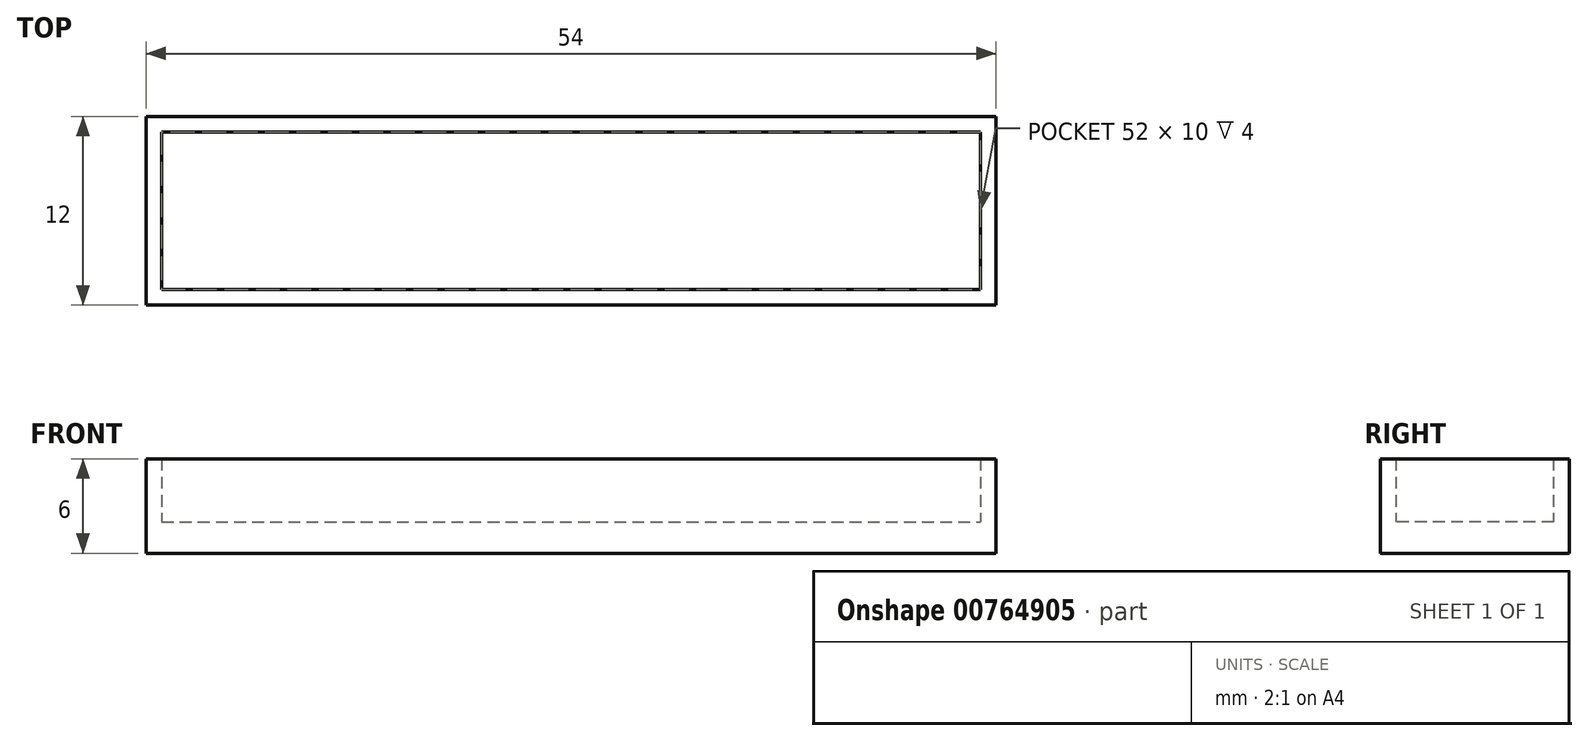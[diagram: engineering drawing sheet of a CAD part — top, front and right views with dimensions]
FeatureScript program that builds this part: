
annotation { "Feature Type Name" : "Feature", "Feature Type Description" : "" }
export const myFeature = defineFeature(function(context is Context, id is Id, definition is map)
    precondition{}
    {
        {
            var Q0;
            Q0=qCreatedBy(makeId("Top.planeOp"),FACE);
            var sketch = newSketch(context, id + "F0", { "sketchPlane" : qUnion([Q0])});
            skLineSegment(sketch, "E0.bottom", {"start": v(-26, 5) * mm, "end": v(26, 5) * mm});
            skLineSegment(sketch, "E0.top", {"start": v(-26, -5) * mm, "end": v(26, -5) * mm});
            skLineSegment(sketch, "E0.left", {"start": v(-26, 5) * mm, "end": v(-26, -5) * mm});
            skLineSegment(sketch, "E0.right", {"start": v(26, 5) * mm, "end": v(26, -5) * mm});
            skPoint(sketch, "E0.middle", {"position": v(0, 0) * mm});
            skLineSegment(sketch, "E1.0", {"start": v(-27, 6) * mm, "end": v(27, 6) * mm});
            skLineSegment(sketch, "E1.1", {"start": v(-27, 6) * mm, "end": v(-27, -6) * mm});
            skLineSegment(sketch, "E1.2", {"start": v(-27, -6) * mm, "end": v(27, -6) * mm});
            skLineSegment(sketch, "E1.3", {"start": v(27, 6) * mm, "end": v(27, -6) * mm});
            skSolve(sketch);
        }
        {
            var Q0;
            Q0=makeQuery(id+"F0.imprint","IMPRINT",FACE,{"disambiguationData":[TD([[makeQuery(id+"F0.imprint","IMPRINT",EDGE,{"derivedFrom":sQuery(id+"F0.wireOp",EDGE,"E0.bottom")}),-1.0]])]});
            extrude(context, id + "F1", {"entities" : qUnion([Q0]), "depth" : 2 * mm, "offsetDistance" : 25 * mm});
        }
        {
            var Q0;
            Q0 = qSketchRegion(id + "F0", true);
            extrude(context, id + "F2", {"entities" : qUnion([Q0]), "operationType" : NewBodyOperationType.ADD, "depth" : 6 * mm, "offsetDistance" : 25 * mm});
        }
    });
